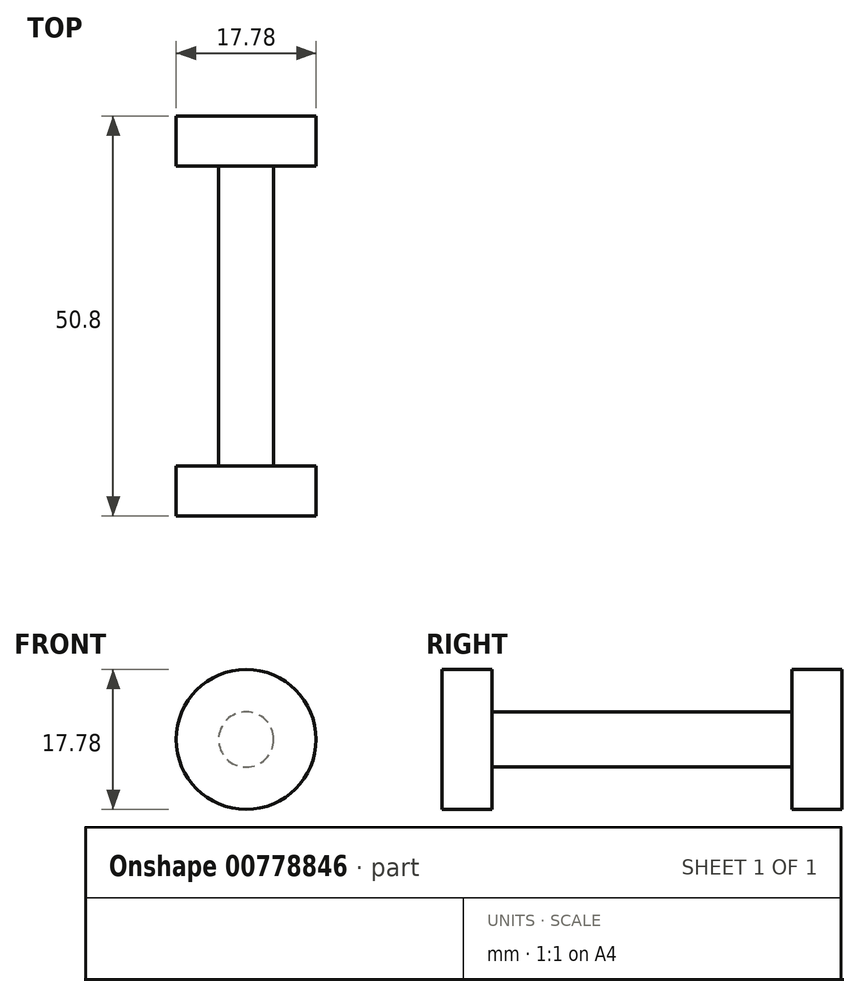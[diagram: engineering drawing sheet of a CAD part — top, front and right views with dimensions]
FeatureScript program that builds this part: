
annotation { "Feature Type Name" : "Feature", "Feature Type Description" : "" }
export const myFeature = defineFeature(function(context is Context, id is Id, definition is map)
    precondition{}
    {
        {
            var Q0;
            Q0=qCreatedBy(makeId("Front.planeOp"),FACE);
            var sketch = newSketch(context, id + "F0", { "sketchPlane" : qUnion([Q0])});
            skCircle(sketch, "E0", {"center": v(0, 0) * mm, "radius": 8.9 * mm});
            skSolve(sketch);
        }
        {
            var Q0;
            Q0=makeQuery(id+"F0.imprint","IMPRINT",FACE,{"disambiguationData":[TD([[makeQuery(id+"F0.imprint","IMPRINT",EDGE,{"derivedFrom":sQuery(id+"F0.wireOp",EDGE,"E0")}),1.0]])]});
            extrude(context, id + "F1", {"entities" : qUnion([Q0]), "depth" : 6.35 * mm, "offsetDistance" : 25.4 * mm});
        }
        {
            var Q0;
            Q0=makeQuery(id+"F1.opExtrude","CAP_FACE",FACE,{"disambiguationData":[OSD([sQuery(id+"F0.wireOp",EDGE,"E0")])],"isStart":false});
            var sketch = newSketch(context, id + "F2", { "sketchPlane" : qUnion([Q0])});
            skCircle(sketch, "E1", {"center": v(0, 0) * mm, "radius": 3.5 * mm});
            skSolve(sketch);
        }
        {
            var Q0;
            Q0=makeQuery(id+"F2.imprint","IMPRINT",FACE,{"disambiguationData":[TD([[makeQuery(id+"F2.imprint","IMPRINT",EDGE,{"derivedFrom":sQuery(id+"F2.wireOp",EDGE,"E1")}),1.0]])]});
            extrude(context, id + "F3", {"entities" : qUnion([Q0]), "depth" : 38.1 * mm, "offsetDistance" : 25.4 * mm});
        }
        {
            var Q0;
            Q0=makeQuery(id+"F3.opExtrude","CAP_FACE",FACE,{"disambiguationData":[OSD([sQuery(id+"F2.wireOp",EDGE,"E1")])],"isStart":false});
            var sketch = newSketch(context, id + "F4", { "sketchPlane" : qUnion([Q0])});
            skCircle(sketch, "E2", {"center": v(0, 0) * mm, "radius": 8.9 * mm});
            skSolve(sketch);
        }
        {
            var Q0;
            Q0 = qSketchRegion(id + "F4", true);
            extrude(context, id + "F5", {"entities" : qUnion([Q0]), "depth" : 6.35 * mm, "offsetDistance" : 25.4 * mm});
        }
    });
